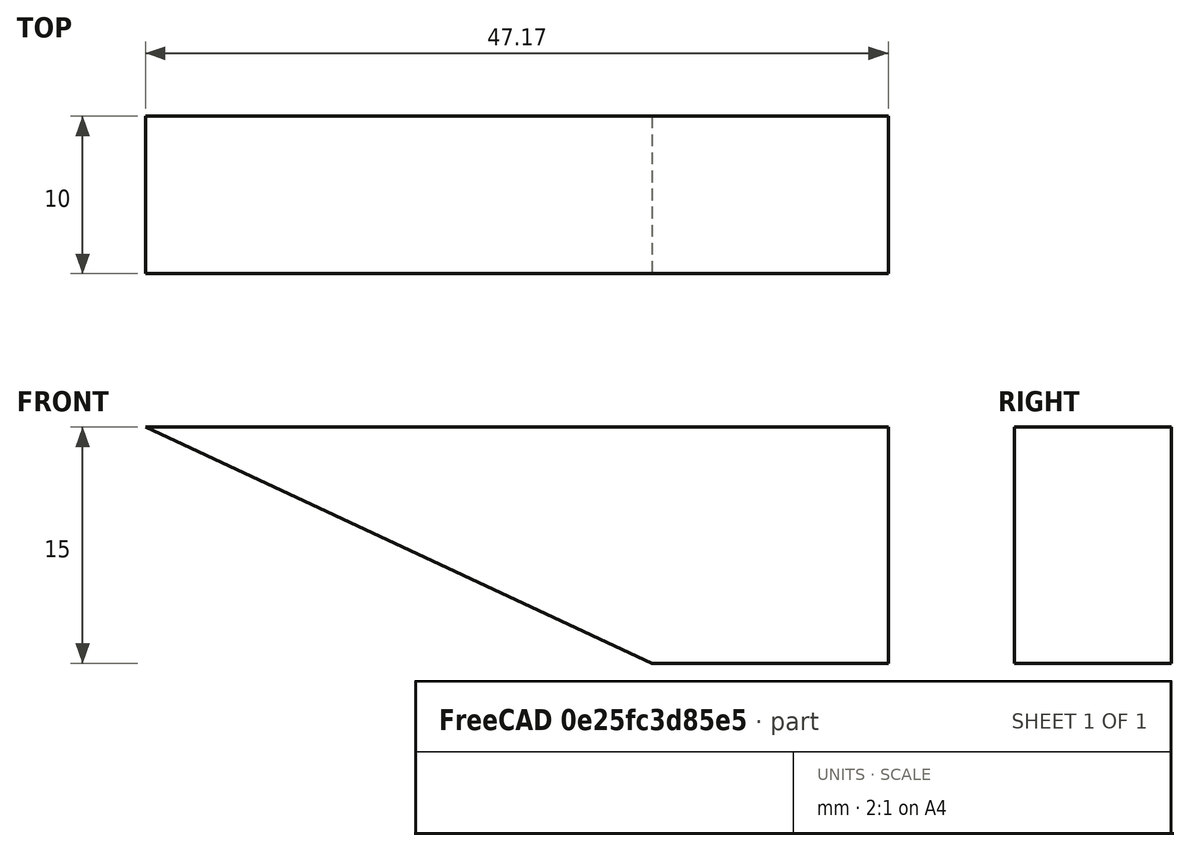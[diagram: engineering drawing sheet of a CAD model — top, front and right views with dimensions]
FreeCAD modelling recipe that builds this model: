
FCSTD DOCUMENT  (FreeCAD 0.19R24366 (Git))
Label: OverhangTest
License: Creative Commons Attribution-NonCommercial-ShareAlike
LicenseURL: http://creativecommons.org/licenses/by-nc-sa/4.0/
objects: Sketcher::SketchObject×1, PartDesign::Pad×1, PartDesign::Body×1
note: 4 computed .brp shape members not serialized (recipe doc carries the construction recipe); baked Part::Feature solids carry a one-line shape summary decoded from their .brp

FEATURE [Sketcher::SketchObject] Sketch
  FullyConstrained = true
  MapMode = 5
  Placement = pos=(0,0,0) rot=(1,0,0;1.5708rad)
  Support = -> [XZ_Plane]
  sketch-geometry (4):
    g0: LineSegment StartX=0 StartY=0 StartZ=0 EndX=15 EndY=0 EndZ=0
    g1: LineSegment StartX=15 StartY=0 StartZ=0 EndX=15 EndY=15 EndZ=0
    g2: LineSegment StartX=15 StartY=15 StartZ=0 EndX=-32.1676 EndY=15 EndZ=0
    g3: LineSegment StartX=-32.1676 StartY=15 StartZ=0 EndX=0 EndY=0 EndZ=0
  constraints (11):
    c: Horizontal(g0)
    c: Coincident(g0,g1)
    c: Vertical(g1)
    c: Coincident(g1,g2)
    c: Horizontal(g2)
    c: Coincident(g2,g3)
    c: Coincident(g3,g0)
    c: Angle(g1,g3) = 1.13446
    c: DistanceY(g1,g1) = 15
    c: DistanceX(g0,g0) = 15
    c: Coincident(g0,g-1)
FEATURE [PartDesign::Pad] Pad
  Direction = (1,1,1)
  Length = 10
  Length2 = 100
  Placement = pos=(0,0,0) rot=(1,0,0;1.5708rad)
  Profile = -> Sketch
  Type = 0
FEATURE [PartDesign::Body] Body
  Group = -> [Sketch,Pad]
  Origin = -> Origin
  Tip = -> Pad
